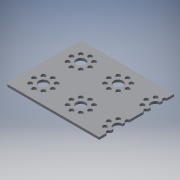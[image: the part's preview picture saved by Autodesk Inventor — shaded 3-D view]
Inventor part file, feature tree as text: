
AUTODESK INVENTOR PART (.ipt)
format: ipt  version: 2019 (Build 230136000, 136)  size: 261,120 bytes
history: native  units: in
note: dims shown in document units (in); Inventor stores cm internally (conversion verified against a paired STEP export)
features: other x1, imported_body x1, extrude x1, sketch x1
ambient origin geometry x8: Origin, YZ Plane, XZ Plane, XY Plane, X Axis, Y Axis, Z Axis, Center Point
bodies: Body1 (feature_tree)
feature tree (4):
  other  "PLATE_64MM_X_192MM_2011"
  imported_body  "Base1"
  extrude  "Extrusion1"  [1 undecoded]
  sketch  "Sketch1"  dims[d0=0.3937in d1=0.0in]
note: 1 required parameter value undecoded (feature->parameter linkage not recoverable at this tier; creation-order binding heuristic only, values carry confidence <= 0.55)
